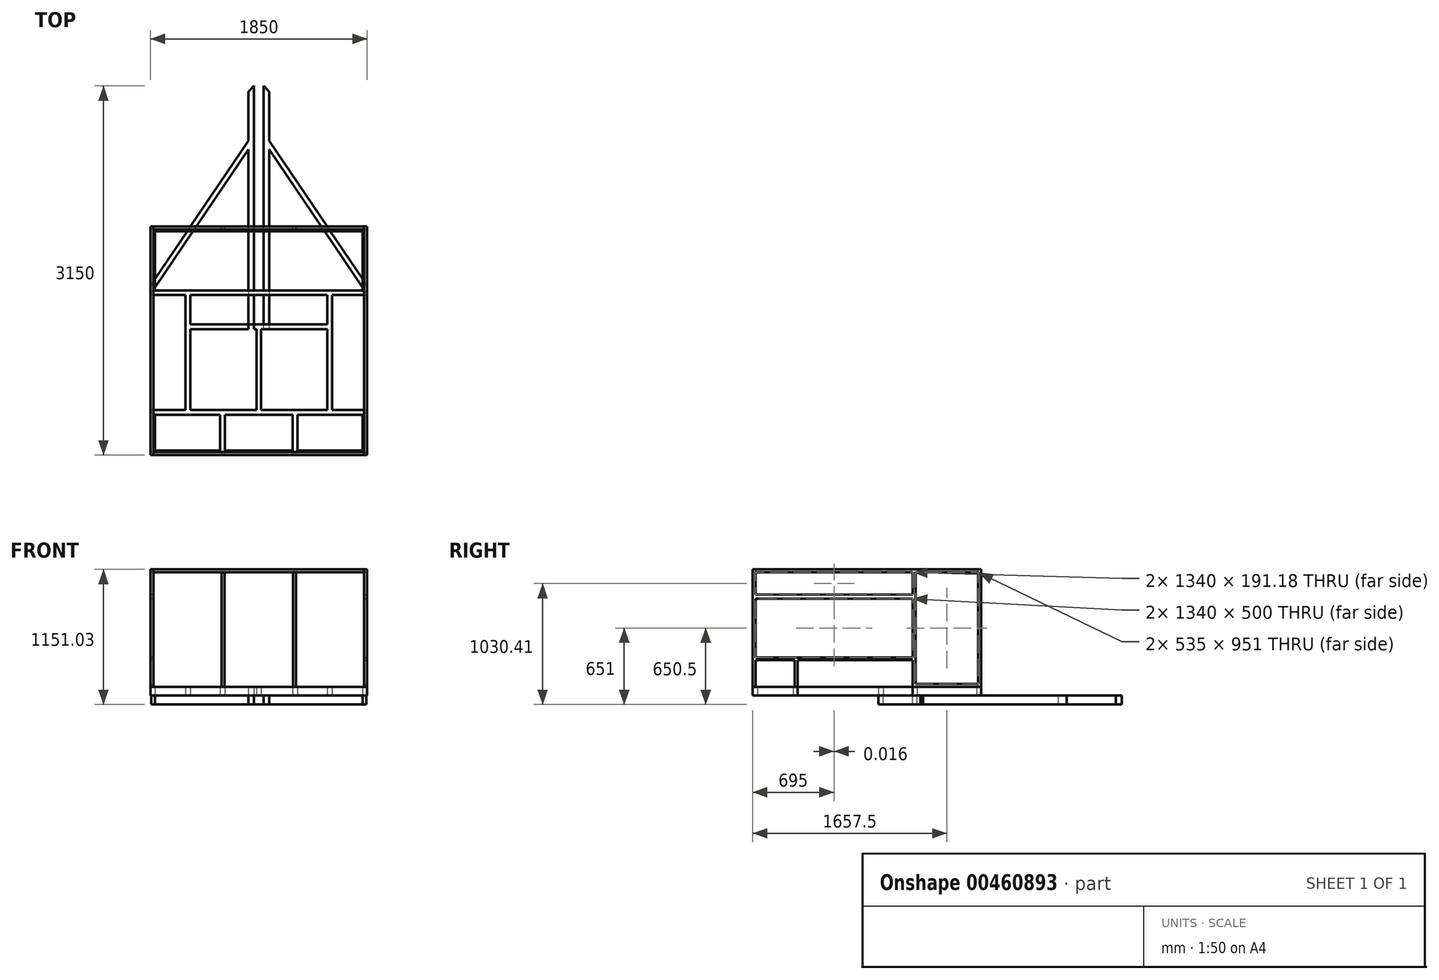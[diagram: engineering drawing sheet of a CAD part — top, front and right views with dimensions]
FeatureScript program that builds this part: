
annotation { "Feature Type Name" : "Feature", "Feature Type Description" : "" }
export const myFeature = defineFeature(function(context is Context, id is Id, definition is map)
    precondition{}
    {
        {
            var Q0;
            Q0=qCreatedBy(makeId("Top.planeOp"),FACE);
            var sketch = newSketch(context, id + "F0", { "sketchPlane" : qUnion([Q0])});
            skLineSegment(sketch, "E0.bottom", {"start": v(0, 0) * mm, "end": v(1850, 0) * mm});
            skLineSegment(sketch, "E0.top", {"start": v(0, -1950) * mm, "end": v(1850, -1950) * mm});
            skLineSegment(sketch, "E1", {"start": v(1850, -585) * mm, "end": v(1850, 0) * mm});
            skLineSegment(sketch, "E2", {"start": v(1850, -1565) * mm, "end": v(1850, -1950) * mm});
            skLineSegment(sketch, "E3", {"start": v(0, -585) * mm, "end": v(0, 0) * mm});
            skLineSegment(sketch, "E4", {"start": v(0, -1565) * mm, "end": v(0, -1950) * mm});
            skLineSegment(sketch, "E5", {"start": v(40, -40) * mm, "end": v(1810, -40) * mm});
            skLineSegment(sketch, "E6", {"start": v(1810, -40) * mm, "end": v(1810, -545) * mm});
            skLineSegment(sketch, "E7", {"start": v(1810, -1605) * mm, "end": v(1810, -1910) * mm});
            skLineSegment(sketch, "E8", {"start": v(1810, -1910) * mm, "end": v(40, -1910) * mm});
            skLineSegment(sketch, "E9", {"start": v(40, -1910) * mm, "end": v(40, -1605) * mm});
            skLineSegment(sketch, "E10", {"start": v(40, -40) * mm, "end": v(40, -545) * mm});
            skLineSegment(sketch, "E11", {"start": v(40, -545) * mm, "end": v(1810, -545) * mm});
            skLineSegment(sketch, "E12", {"start": v(0, -585) * mm, "end": v(1850, -585) * mm});
            skLineSegment(sketch, "E13", {"start": v(300, -1565) * mm, "end": v(300, -585) * mm});
            skLineSegment(sketch, "E14", {"start": v(1550, -1565) * mm, "end": v(1550, -585) * mm});
            skLineSegment(sketch, "E15", {"start": v(40, -1605) * mm, "end": v(1810, -1605) * mm});
            skLineSegment(sketch, "E16", {"start": v(0, -1565) * mm, "end": v(1850, -1565) * mm});
            skLineSegment(sketch, "E17", {"start": v(340, -585) * mm, "end": v(340, -1565) * mm});
            skLineSegment(sketch, "E18", {"start": v(1510, -585) * mm, "end": v(1510, -1565) * mm});
            skLineSegment(sketch, "E19", {"start": v(40, -518.74) * mm, "end": v(835, 659) * mm});
            skLineSegment(sketch, "E20", {"start": v(1810, -518.74) * mm, "end": v(1015, 659) * mm});
            skLineSegment(sketch, "E21", {"start": v(1810, -518.74) * mm, "end": v(1843.15, -496.36) * mm});
            skLineSegment(sketch, "E22", {"start": v(1843.15, -496.36) * mm, "end": v(1015, 730.5) * mm});
            skLineSegment(sketch, "E23", {"start": v(1015, 730.5) * mm, "end": v(1015, 659) * mm});
            skLineSegment(sketch, "E24", {"start": v(40, -518.74) * mm, "end": v(6.85, -496.36) * mm});
            skLineSegment(sketch, "E25", {"start": v(6.85, -496.36) * mm, "end": v(835, 730.5) * mm});
            skLineSegment(sketch, "E26", {"start": v(835, 730.5) * mm, "end": v(835, 659) * mm});
            skLineSegment(sketch, "E27", {"start": v(340, -835.42) * mm, "end": v(1510, -835.42) * mm});
            skLineSegment(sketch, "E28", {"start": v(340, -875.42) * mm, "end": v(1510, -875.42) * mm});
            skLineSegment(sketch, "E29", {"start": v(905, -875.42) * mm, "end": v(905, -1565) * mm});
            skLineSegment(sketch, "E30", {"start": v(945, -875.42) * mm, "end": v(945, -1565) * mm});
            skLineSegment(sketch, "E31", {"start": v(595, -1605) * mm, "end": v(595, -1910) * mm});
            skLineSegment(sketch, "E32", {"start": v(635, -1605) * mm, "end": v(635, -1910) * mm});
            skLineSegment(sketch, "E33", {"start": v(1215, -1605) * mm, "end": v(1215, -1910) * mm});
            skLineSegment(sketch, "E34", {"start": v(1255, -1605) * mm, "end": v(1255, -1910) * mm});
            skLineSegment(sketch, "E35", {"start": v(835, -875.42) * mm, "end": v(885, -875.42) * mm});
            skLineSegment(sketch, "E36", {"start": v(885, -875.42) * mm, "end": v(885, 1200) * mm});
            skLineSegment(sketch, "E37", {"start": v(965, -875.42) * mm, "end": v(965, 1200) * mm});
            skLineSegment(sketch, "E38", {"start": v(885, 1200) * mm, "end": v(835, 1150) * mm});
            skLineSegment(sketch, "E39", {"start": v(965, 1200) * mm, "end": v(1015, 1150) * mm});
            skLineSegment(sketch, "E40", {"start": v(835, 1150) * mm, "end": v(835, -875.42) * mm});
            skLineSegment(sketch, "E41", {"start": v(1015, 1150) * mm, "end": v(1015, -875.42) * mm});
            skSolve(sketch);
        }
        {
            var Q0;
            {var subQ0=sQuery(id+"F0.wireOp",EDGE,"E19");var subQ1=sQuery(id+"F0.wireOp",EDGE,"E0.bottom");var subQ2=makeQuery(id+"F0.imprint","INTERSECT",VERTEX,{"derivedFrom":[subQ1,subQ0]});Q0=makeQuery(id+"F0.imprint","IMPRINT",FACE,{"disambiguationData":[TD([[makeQuery(id+"F0.imprint","IMPRINT",EDGE,{"disambiguationData":[TD([[subQ2,-1.0]])],"derivedFrom":subQ1}),-1.0]])]});}
            var Q1;
            {var subQ0=sQuery(id+"F0.wireOp",EDGE,"E36");var subQ1=sQuery(id+"F0.wireOp",EDGE,"E0.bottom");var subQ2=makeQuery(id+"F0.imprint","INTERSECT",VERTEX,{"derivedFrom":[subQ1,subQ0]});Q1=makeQuery(id+"F0.imprint","IMPRINT",FACE,{"disambiguationData":[TD([[makeQuery(id+"F0.imprint","IMPRINT",EDGE,{"disambiguationData":[TD([[subQ2,1.0]])],"derivedFrom":subQ1}),-1.0]])]});}
            var Q2;
            {var subQ0=sQuery(id+"F0.wireOp",EDGE,"E36");var subQ1=sQuery(id+"F0.wireOp",EDGE,"E0.bottom");var subQ2=makeQuery(id+"F0.imprint","INTERSECT",VERTEX,{"derivedFrom":[subQ1,subQ0]});Q2=makeQuery(id+"F0.imprint","IMPRINT",FACE,{"disambiguationData":[TD([[makeQuery(id+"F0.imprint","IMPRINT",EDGE,{"disambiguationData":[TD([[subQ2,-1.0]])],"derivedFrom":subQ1}),-1.0]])]});}
            var Q3;
            {var subQ0=sQuery(id+"F0.wireOp",EDGE,"E37");var subQ1=sQuery(id+"F0.wireOp",EDGE,"E0.bottom");var subQ2=makeQuery(id+"F0.imprint","INTERSECT",VERTEX,{"derivedFrom":[subQ1,subQ0]});Q3=makeQuery(id+"F0.imprint","IMPRINT",FACE,{"disambiguationData":[TD([[makeQuery(id+"F0.imprint","IMPRINT",EDGE,{"disambiguationData":[TD([[subQ2,-1.0]])],"derivedFrom":subQ1}),-1.0]])]});}
            var Q4;
            {var subQ0=sQuery(id+"F0.wireOp",EDGE,"09ETFbxQ-A6C1-cuEm-suVw-SmpEZGGyVelw");var subQ1=sQuery(id+"F0.wireOp",EDGE,"E0.bottom");var subQ2=makeQuery(id+"F0.imprint","INTERSECT",VERTEX,{"derivedFrom":[subQ1,subQ0]});Q4=makeQuery(id+"F0.imprint","IMPRINT",FACE,{"disambiguationData":[TD([[makeQuery(id+"F0.imprint","IMPRINT",EDGE,{"disambiguationData":[TD([[subQ2,-1.0]])],"derivedFrom":subQ1}),-1.0]])]});}
            var Q5;
            {var subQ0=sQuery(id+"F0.wireOp",EDGE,"E25");var subQ1=sQuery(id+"F0.wireOp",EDGE,"E0.bottom");var subQ2=makeQuery(id+"F0.imprint","INTERSECT",VERTEX,{"derivedFrom":[subQ1,subQ0]});Q5=makeQuery(id+"F0.imprint","IMPRINT",FACE,{"disambiguationData":[TD([[makeQuery(id+"F0.imprint","IMPRINT",EDGE,{"disambiguationData":[TD([[subQ2,-1.0]])],"derivedFrom":subQ1}),-1.0]])]});}
            var Q6;
            {var subQ4=sQuery(id+"F0.wireOp",EDGE,"E3");Q6=makeQuery(id+"F0.imprint","IMPRINT",FACE,{"disambiguationData":[TD([[makeQuery(id+"F0.imprint","IMPRINT",EDGE,{"derivedFrom":subQ4}),-1.0]])]});}
            var Q7;
            {var subQ0=sQuery(id+"F0.wireOp",EDGE,"E22");var subQ1=sQuery(id+"F0.wireOp",EDGE,"E0.bottom");var subQ2=makeQuery(id+"F0.imprint","INTERSECT",VERTEX,{"derivedFrom":[subQ1,subQ0]});Q7=makeQuery(id+"F0.imprint","IMPRINT",FACE,{"disambiguationData":[TD([[makeQuery(id+"F0.imprint","IMPRINT",EDGE,{"disambiguationData":[TD([[subQ2,1.0]])],"derivedFrom":subQ1}),-1.0]])]});}
            var Q8;
            {var subQ1=sQuery(id+"F0.wireOp",EDGE,"E1");Q8=makeQuery(id+"F0.imprint","IMPRINT",FACE,{"disambiguationData":[TD([[makeQuery(id+"F0.imprint","IMPRINT",EDGE,{"derivedFrom":subQ1}),1.0]])]});}
            var Q9;
            {var subQ0=sQuery(id+"F0.wireOp",EDGE,"E37");var subQ1=sQuery(id+"F0.wireOp",EDGE,"E11");var subQ2=makeQuery(id+"F0.imprint","INTERSECT",VERTEX,{"derivedFrom":[subQ1,subQ0]});Q9=makeQuery(id+"F0.imprint","IMPRINT",FACE,{"disambiguationData":[TD([[makeQuery(id+"F0.imprint","IMPRINT",EDGE,{"disambiguationData":[TD([[subQ2,-1.0]])],"derivedFrom":subQ1}),-1.0]])]});}
            var Q10;
            {var subQ0=sQuery(id+"F0.wireOp",EDGE,"E36");var subQ1=sQuery(id+"F0.wireOp",EDGE,"E11");var subQ2=makeQuery(id+"F0.imprint","INTERSECT",VERTEX,{"derivedFrom":[subQ1,subQ0]});Q10=makeQuery(id+"F0.imprint","IMPRINT",FACE,{"disambiguationData":[TD([[makeQuery(id+"F0.imprint","IMPRINT",EDGE,{"disambiguationData":[TD([[subQ2,-1.0]])],"derivedFrom":subQ1}),-1.0]])]});}
            var Q11;
            {var subQ0=sQuery(id+"F0.wireOp",EDGE,"pQNNPpNY-eGQG-TIMN-oy4P-XU9trb4b4uZt");var subQ1=sQuery(id+"F0.wireOp",EDGE,"E11");var subQ2=makeQuery(id+"F0.imprint","INTERSECT",VERTEX,{"derivedFrom":[subQ1,subQ0]});Q11=makeQuery(id+"F0.imprint","IMPRINT",FACE,{"disambiguationData":[TD([[makeQuery(id+"F0.imprint","IMPRINT",EDGE,{"disambiguationData":[TD([[subQ2,-1.0]])],"derivedFrom":subQ1}),-1.0]])]});}
            var Q12;
            {var subQ0=sQuery(id+"F0.wireOp",EDGE,"E27");var subQ1=sQuery(id+"F0.wireOp",EDGE,"E17");var subQ2=makeQuery(id+"F0.imprint","INTERSECT",VERTEX,{"derivedFrom":[subQ1,subQ0]});Q12=makeQuery(id+"F0.imprint","IMPRINT",FACE,{"disambiguationData":[TD([[makeQuery(id+"F0.imprint","IMPRINT",EDGE,{"disambiguationData":[TD([[subQ2,-1.0]])],"derivedFrom":subQ1}),1.0]])]});}
            var Q13;
            {var subQ5=sQuery(id+"F0.wireOp",EDGE,"E35");Q13=makeQuery(id+"F0.imprint","IMPRINT",FACE,{"disambiguationData":[TD([[makeQuery(id+"F0.imprint","IMPRINT",EDGE,{"derivedFrom":subQ5}),1.0]])]});}
            var Q14;
            {var subQ5=sQuery(id+"F0.wireOp",EDGE,"E36");var subQ7=sQuery(id+"F0.wireOp",EDGE,"E27");var subQ8=makeQuery(id+"F0.imprint","INTERSECT",VERTEX,{"derivedFrom":[subQ7,subQ5]});Q14=makeQuery(id+"F0.imprint","IMPRINT",FACE,{"disambiguationData":[TD([[makeQuery(id+"F0.imprint","IMPRINT",EDGE,{"disambiguationData":[TD([[subQ8,-1.0]])],"derivedFrom":subQ7}),-1.0]])]});}
            var Q15;
            {var subQ0=sQuery(id+"F0.wireOp",EDGE,"E37");var subQ1=sQuery(id+"F0.wireOp",EDGE,"E27");var subQ2=makeQuery(id+"F0.imprint","INTERSECT",VERTEX,{"derivedFrom":[subQ1,subQ0]});Q15=makeQuery(id+"F0.imprint","IMPRINT",FACE,{"disambiguationData":[TD([[makeQuery(id+"F0.imprint","IMPRINT",EDGE,{"disambiguationData":[TD([[subQ2,-1.0]])],"derivedFrom":subQ1}),-1.0]])]});}
            var Q16;
            {var subQ0=sQuery(id+"F0.wireOp",EDGE,"E27");var subQ1=sQuery(id+"F0.wireOp",EDGE,"E18");var subQ2=makeQuery(id+"F0.imprint","INTERSECT",VERTEX,{"derivedFrom":[subQ1,subQ0]});Q16=makeQuery(id+"F0.imprint","IMPRINT",FACE,{"disambiguationData":[TD([[makeQuery(id+"F0.imprint","IMPRINT",EDGE,{"disambiguationData":[TD([[subQ2,-1.0]])],"derivedFrom":subQ1}),-1.0]])]});}
            var Q17;
            {var subQ5=sQuery(id+"F0.wireOp",EDGE,"E14");Q17=makeQuery(id+"F0.imprint","IMPRINT",FACE,{"disambiguationData":[TD([[makeQuery(id+"F0.imprint","IMPRINT",EDGE,{"derivedFrom":subQ5}),1.0]])]});}
            var Q18;
            {var subQ4=sQuery(id+"F0.wireOp",EDGE,"E13");Q18=makeQuery(id+"F0.imprint","IMPRINT",FACE,{"disambiguationData":[TD([[makeQuery(id+"F0.imprint","IMPRINT",EDGE,{"derivedFrom":subQ4}),-1.0]])]});}
            var Q19;
            {var subQ0=sQuery(id+"F0.wireOp",EDGE,"E29");Q19=makeQuery(id+"F0.imprint","IMPRINT",FACE,{"disambiguationData":[TD([[makeQuery(id+"F0.imprint","IMPRINT",EDGE,{"derivedFrom":subQ0}),1.0]])]});}
            var Q20;
            Q20=makeQuery(id+"F0.imprint","IMPRINT",FACE,{"disambiguationData":[TD([[makeQuery(id+"F0.imprint","IMPRINT",EDGE,{"derivedFrom":sQuery(id+"F0.wireOp",EDGE,"E0.top")}),1.0]])]});
            var Q21;
            {var subQ0=sQuery(id+"F0.wireOp",EDGE,"E31");Q21=makeQuery(id+"F0.imprint","IMPRINT",FACE,{"disambiguationData":[TD([[makeQuery(id+"F0.imprint","IMPRINT",EDGE,{"derivedFrom":subQ0}),1.0]])]});}
            var Q22;
            {var subQ0=sQuery(id+"F0.wireOp",EDGE,"E33");Q22=makeQuery(id+"F0.imprint","IMPRINT",FACE,{"disambiguationData":[TD([[makeQuery(id+"F0.imprint","IMPRINT",EDGE,{"derivedFrom":subQ0}),1.0]])]});}
            var Q23;
            {var subQ0=sQuery(id+"F0.wireOp",EDGE,"E21");Q23=makeQuery(id+"F0.imprint","IMPRINT",FACE,{"disambiguationData":[TD([[makeQuery(id+"F0.imprint","IMPRINT",EDGE,{"derivedFrom":subQ0}),1.0]])]});}
            var Q24;
            {var subQ0=sQuery(id+"F0.wireOp",EDGE,"E24");Q24=makeQuery(id+"F0.imprint","IMPRINT",FACE,{"disambiguationData":[TD([[makeQuery(id+"F0.imprint","IMPRINT",EDGE,{"derivedFrom":subQ0}),-1.0]])]});}
            extrude(context, id + "F1", {"entities" : qUnion([Q0, Q1, Q2, Q3, Q4, Q5, Q6, Q7, Q8, Q9, Q10, Q11, Q12, Q13, Q14, Q15, Q16, Q17, Q18, Q19, Q20, Q21, Q22, Q23, Q24]), "depth" : 75 * mm});
        }
        {
            var Q0;
            {var subQ0=sQuery(id+"F0.wireOp",EDGE,"E37");var subQ1=sQuery(id+"F0.wireOp",EDGE,"E12");var subQ2=makeQuery(id+"F0.imprint","INTERSECT",VERTEX,{"derivedFrom":[subQ1,subQ0]});Q0=makeQuery(id+"F0.imprint","IMPRINT",FACE,{"disambiguationData":[TD([[makeQuery(id+"F0.imprint","IMPRINT",EDGE,{"disambiguationData":[TD([[subQ2,-1.0]])],"derivedFrom":subQ1}),-1.0]])]});}
            var Q1;
            {var subQ0=sQuery(id+"F0.wireOp",EDGE,"E25");var subQ1=sQuery(id+"F0.wireOp",EDGE,"E0.bottom");var subQ2=makeQuery(id+"F0.imprint","INTERSECT",VERTEX,{"derivedFrom":[subQ1,subQ0]});Q1=makeQuery(id+"F0.imprint","IMPRINT",FACE,{"disambiguationData":[TD([[makeQuery(id+"F0.imprint","IMPRINT",EDGE,{"disambiguationData":[TD([[subQ2,-1.0]])],"derivedFrom":subQ1}),1.0]])]});}
            var Q2;
            {var subQ0=sQuery(id+"F0.wireOp",EDGE,"E25");var subQ1=sQuery(id+"F0.wireOp",EDGE,"E5");var subQ2=makeQuery(id+"F0.imprint","INTERSECT",VERTEX,{"derivedFrom":[subQ1,subQ0]});Q2=makeQuery(id+"F0.imprint","IMPRINT",FACE,{"disambiguationData":[TD([[makeQuery(id+"F0.imprint","IMPRINT",EDGE,{"disambiguationData":[TD([[subQ2,-1.0]])],"derivedFrom":subQ1}),-1.0]])]});}
            var Q3;
            {var subQ0=sQuery(id+"F0.wireOp",EDGE,"E25");var subQ1=sQuery(id+"F0.wireOp",EDGE,"E0.bottom");var subQ2=makeQuery(id+"F0.imprint","INTERSECT",VERTEX,{"derivedFrom":[subQ1,subQ0]});Q3=makeQuery(id+"F0.imprint","IMPRINT",FACE,{"disambiguationData":[TD([[makeQuery(id+"F0.imprint","IMPRINT",EDGE,{"disambiguationData":[TD([[subQ2,-1.0]])],"derivedFrom":subQ1}),-1.0]])]});}
            var Q4;
            {var subQ0=sQuery(id+"F0.wireOp",EDGE,"E37");var subQ1=sQuery(id+"F0.wireOp",EDGE,"E5");var subQ2=makeQuery(id+"F0.imprint","INTERSECT",VERTEX,{"derivedFrom":[subQ1,subQ0]});Q4=makeQuery(id+"F0.imprint","IMPRINT",FACE,{"disambiguationData":[TD([[makeQuery(id+"F0.imprint","IMPRINT",EDGE,{"disambiguationData":[TD([[subQ2,-1.0]])],"derivedFrom":subQ1}),-1.0]])]});}
            var Q5;
            {var subQ0=sQuery(id+"F0.wireOp",EDGE,"E20");var subQ1=sQuery(id+"F0.wireOp",EDGE,"E5");var subQ2=makeQuery(id+"F0.imprint","INTERSECT",VERTEX,{"derivedFrom":[subQ1,subQ0]});Q5=makeQuery(id+"F0.imprint","IMPRINT",FACE,{"disambiguationData":[TD([[makeQuery(id+"F0.imprint","IMPRINT",EDGE,{"disambiguationData":[TD([[subQ2,-1.0]])],"derivedFrom":subQ1}),-1.0]])]});}
            var Q6;
            {var subQ0=sQuery(id+"F0.wireOp",EDGE,"E22");var subQ1=sQuery(id+"F0.wireOp",EDGE,"E0.bottom");var subQ2=makeQuery(id+"F0.imprint","INTERSECT",VERTEX,{"derivedFrom":[subQ1,subQ0]});Q6=makeQuery(id+"F0.imprint","IMPRINT",FACE,{"disambiguationData":[TD([[makeQuery(id+"F0.imprint","IMPRINT",EDGE,{"disambiguationData":[TD([[subQ2,1.0]])],"derivedFrom":subQ1}),1.0]])]});}
            var Q7;
            {var subQ0=sQuery(id+"F0.wireOp",EDGE,"E22");var subQ1=sQuery(id+"F0.wireOp",EDGE,"E0.bottom");var subQ2=makeQuery(id+"F0.imprint","INTERSECT",VERTEX,{"derivedFrom":[subQ1,subQ0]});Q7=makeQuery(id+"F0.imprint","IMPRINT",FACE,{"disambiguationData":[TD([[makeQuery(id+"F0.imprint","IMPRINT",EDGE,{"disambiguationData":[TD([[subQ2,1.0]])],"derivedFrom":subQ1}),-1.0]])]});}
            var Q8;
            {var subQ0=sQuery(id+"F0.wireOp",EDGE,"E37");var subQ1=sQuery(id+"F0.wireOp",EDGE,"E0.bottom");var subQ2=makeQuery(id+"F0.imprint","INTERSECT",VERTEX,{"derivedFrom":[subQ1,subQ0]});Q8=makeQuery(id+"F0.imprint","IMPRINT",FACE,{"disambiguationData":[TD([[makeQuery(id+"F0.imprint","IMPRINT",EDGE,{"disambiguationData":[TD([[subQ2,-1.0]])],"derivedFrom":subQ1}),-1.0]])]});}
            var Q9;
            {var subQ0=sQuery(id+"F0.wireOp",EDGE,"E36");var subQ1=sQuery(id+"F0.wireOp",EDGE,"E0.bottom");var subQ2=makeQuery(id+"F0.imprint","INTERSECT",VERTEX,{"derivedFrom":[subQ1,subQ0]});Q9=makeQuery(id+"F0.imprint","IMPRINT",FACE,{"disambiguationData":[TD([[makeQuery(id+"F0.imprint","IMPRINT",EDGE,{"disambiguationData":[TD([[subQ2,1.0]])],"derivedFrom":subQ1}),-1.0]])]});}
            var Q10;
            {var subQ0=sQuery(id+"F0.wireOp",EDGE,"E40");var subQ1=sQuery(id+"F0.wireOp",EDGE,"E11");var subQ2=makeQuery(id+"F0.imprint","INTERSECT",VERTEX,{"derivedFrom":[subQ1,subQ0]});Q10=makeQuery(id+"F0.imprint","IMPRINT",FACE,{"disambiguationData":[TD([[makeQuery(id+"F0.imprint","IMPRINT",EDGE,{"disambiguationData":[TD([[subQ2,-1.0]])],"derivedFrom":subQ1}),-1.0]])]});}
            var Q11;
            {var subQ0=sQuery(id+"F0.wireOp",EDGE,"E36");var subQ1=sQuery(id+"F0.wireOp",EDGE,"E11");var subQ2=makeQuery(id+"F0.imprint","INTERSECT",VERTEX,{"derivedFrom":[subQ1,subQ0]});Q11=makeQuery(id+"F0.imprint","IMPRINT",FACE,{"disambiguationData":[TD([[makeQuery(id+"F0.imprint","IMPRINT",EDGE,{"disambiguationData":[TD([[subQ2,-1.0]])],"derivedFrom":subQ1}),-1.0]])]});}
            var Q12;
            {var subQ0=sQuery(id+"F0.wireOp",EDGE,"E37");var subQ1=sQuery(id+"F0.wireOp",EDGE,"E11");var subQ2=makeQuery(id+"F0.imprint","INTERSECT",VERTEX,{"derivedFrom":[subQ1,subQ0]});Q12=makeQuery(id+"F0.imprint","IMPRINT",FACE,{"disambiguationData":[TD([[makeQuery(id+"F0.imprint","IMPRINT",EDGE,{"disambiguationData":[TD([[subQ2,-1.0]])],"derivedFrom":subQ1}),-1.0]])]});}
            var Q13;
            {var subQ0=sQuery(id+"F0.wireOp",EDGE,"E37");var subQ1=sQuery(id+"F0.wireOp",EDGE,"E12");var subQ2=makeQuery(id+"F0.imprint","INTERSECT",VERTEX,{"derivedFrom":[subQ1,subQ0]});Q13=makeQuery(id+"F0.imprint","IMPRINT",FACE,{"disambiguationData":[TD([[makeQuery(id+"F0.imprint","IMPRINT",EDGE,{"disambiguationData":[TD([[subQ2,-1.0]])],"derivedFrom":subQ1}),-1.0]])]});}
            var Q14;
            {var subQ5=sQuery(id+"F0.wireOp",EDGE,"E35");Q14=makeQuery(id+"F0.imprint","IMPRINT",FACE,{"disambiguationData":[TD([[makeQuery(id+"F0.imprint","IMPRINT",EDGE,{"derivedFrom":subQ5}),1.0]])]});}
            var Q15;
            {var subQ0=sQuery(id+"F0.wireOp",EDGE,"E37");var subQ1=sQuery(id+"F0.wireOp",EDGE,"E27");var subQ2=makeQuery(id+"F0.imprint","INTERSECT",VERTEX,{"derivedFrom":[subQ1,subQ0]});Q15=makeQuery(id+"F0.imprint","IMPRINT",FACE,{"disambiguationData":[TD([[makeQuery(id+"F0.imprint","IMPRINT",EDGE,{"disambiguationData":[TD([[subQ2,-1.0]])],"derivedFrom":subQ1}),-1.0]])]});}
            var Q16;
            {var subQ0=sQuery(id+"F0.wireOp",EDGE,"E24");Q16=makeQuery(id+"F0.imprint","IMPRINT",FACE,{"disambiguationData":[TD([[makeQuery(id+"F0.imprint","IMPRINT",EDGE,{"derivedFrom":subQ0}),-1.0]])]});}
            var Q17;
            {var subQ0=sQuery(id+"F0.wireOp",EDGE,"E37");var subQ1=sQuery(id+"F0.wireOp",EDGE,"E11");var subQ2=makeQuery(id+"F0.imprint","INTERSECT",VERTEX,{"derivedFrom":[subQ1,subQ0]});Q17=makeQuery(id+"F0.imprint","IMPRINT",FACE,{"disambiguationData":[TD([[makeQuery(id+"F0.imprint","IMPRINT",EDGE,{"disambiguationData":[TD([[subQ2,-1.0]])],"derivedFrom":subQ1}),-1.0]])]});}
            var Q18;
            {var subQ0=sQuery(id+"F0.wireOp",EDGE,"E21");Q18=makeQuery(id+"F0.imprint","IMPRINT",FACE,{"disambiguationData":[TD([[makeQuery(id+"F0.imprint","IMPRINT",EDGE,{"derivedFrom":subQ0}),1.0]])]});}
            var Q19;
            {var subQ0=sQuery(id+"F0.wireOp",EDGE,"E40");var subQ1=sQuery(id+"F0.wireOp",EDGE,"E5");var subQ2=makeQuery(id+"F0.imprint","INTERSECT",VERTEX,{"derivedFrom":[subQ1,subQ0]});Q19=makeQuery(id+"F0.imprint","IMPRINT",FACE,{"disambiguationData":[TD([[makeQuery(id+"F0.imprint","IMPRINT",EDGE,{"disambiguationData":[TD([[subQ2,-1.0]])],"derivedFrom":subQ1}),-1.0]])]});}
            var Q20;
            {var subQ0=sQuery(id+"F0.wireOp",EDGE,"E40");var subQ1=sQuery(id+"F0.wireOp",EDGE,"E12");var subQ2=makeQuery(id+"F0.imprint","INTERSECT",VERTEX,{"derivedFrom":[subQ1,subQ0]});Q20=makeQuery(id+"F0.imprint","IMPRINT",FACE,{"disambiguationData":[TD([[makeQuery(id+"F0.imprint","IMPRINT",EDGE,{"disambiguationData":[TD([[subQ2,-1.0]])],"derivedFrom":subQ1}),-1.0]])]});}
            var Q21;
            {var subQ0=sQuery(id+"F0.wireOp",EDGE,"E38");Q21=makeQuery(id+"F0.imprint","IMPRINT",FACE,{"disambiguationData":[TD([[makeQuery(id+"F0.imprint","IMPRINT",EDGE,{"derivedFrom":subQ0}),1.0]])]});}
            var Q22;
            {var subQ2=sQuery(id+"F0.wireOp",EDGE,"E39");Q22=makeQuery(id+"F0.imprint","IMPRINT",FACE,{"disambiguationData":[TD([[makeQuery(id+"F0.imprint","IMPRINT",EDGE,{"derivedFrom":subQ2}),-1.0]])]});}
            extrude(context, id + "F2", {"entities" : qUnion([Q0, Q1, Q2, Q3, Q4, Q5, Q6, Q7, Q8, Q9, Q10, Q11, Q12, Q13, Q14, Q15, Q16, Q17, Q18, Q19, Q20, Q21, Q22]), "oppositeDirection" : true, "depth" : 75 * mm});
        }
        {
            var Q0;
            Q0=qCreatedBy(makeId("Right.planeOp"),FACE);
            var sketch = newSketch(context, id + "F3", { "sketchPlane" : qUnion([Q0])});
            skLineSegment(sketch, "E42.top", {"start": v(0, 1076) * mm, "end": v(-1950, 1076) * mm});
            skLineSegment(sketch, "E42.left", {"start": v(0, 75) * mm, "end": v(0, 1076) * mm});
            skLineSegment(sketch, "E42.right", {"start": v(-1950, 76) * mm, "end": v(-1950, 1076) * mm});
            skLineSegment(sketch, "E43.bottom", {"start": v(-25, 1051) * mm, "end": v(-1925, 1051) * mm});
            skLineSegment(sketch, "E43.left", {"start": v(-25, 1051) * mm, "end": v(-25, 100) * mm});
            skLineSegment(sketch, "E43.right", {"start": v(-1925, 1051) * mm, "end": v(-1925, 76) * mm});
            skLineSegment(sketch, "E44", {"start": v(-585, 75) * mm, "end": v(-585, 1051) * mm});
            skLineSegment(sketch, "E45", {"start": v(-25, 100) * mm, "end": v(-560, 100) * mm});
            skLineSegment(sketch, "E46", {"start": v(-560, 100) * mm, "end": v(-560, 1051) * mm});
            skLineSegment(sketch, "E47", {"start": v(-585, 326) * mm, "end": v(-1925, 326) * mm});
            skLineSegment(sketch, "E48", {"start": v(-585, 301) * mm, "end": v(-1925, 301) * mm});
            skLineSegment(sketch, "E49", {"start": v(-585, 75) * mm, "end": v(0, 75) * mm});
            skLineSegment(sketch, "E50", {"start": v(-1925, 76) * mm, "end": v(-1950, 76) * mm});
            skLineSegment(sketch, "E51", {"start": v(-1565, 75.02) * mm, "end": v(-1565, 301) * mm});
            skLineSegment(sketch, "E52", {"start": v(-1565, 301) * mm, "end": v(-1590, 301) * mm});
            skLineSegment(sketch, "E53", {"start": v(-1590, 301) * mm, "end": v(-1590, 75.02) * mm});
            skLineSegment(sketch, "E54", {"start": v(-1590, 75.02) * mm, "end": v(-1565, 75.02) * mm});
            skLineSegment(sketch, "E55", {"start": v(-585, 826) * mm, "end": v(-1925, 826) * mm});
            skLineSegment(sketch, "E56", {"start": v(-585, 826) * mm, "end": v(-585, 859.82) * mm});
            skLineSegment(sketch, "E57", {"start": v(-585, 859.82) * mm, "end": v(-1925, 859.82) * mm});
            skLineSegment(sketch, "E58", {"start": v(-1925, 859.82) * mm, "end": v(-1925, 826) * mm});
            skSolve(sketch);
        }
        {
            var Q0;
            Q0=makeQuery(id+"F3.imprint","IMPRINT",FACE,{"disambiguationData":[TD([[makeQuery(id+"F3.imprint","IMPRINT",EDGE,{"derivedFrom":sQuery(id+"F3.wireOp",EDGE,"E42.top")}),1.0]])]});
            var Q1;
            {var subQ0=sQuery(id+"F3.wireOp",EDGE,"E47");Q1=makeQuery(id+"F3.imprint","IMPRINT",FACE,{"disambiguationData":[TD([[makeQuery(id+"F3.imprint","IMPRINT",EDGE,{"derivedFrom":subQ0}),1.0]])]});}
            var Q2;
            Q2=makeQuery(id+"F3.imprint","IMPRINT",FACE,{"disambiguationData":[TD([[makeQuery(id+"F3.imprint","IMPRINT",EDGE,{"derivedFrom":sQuery(id+"F3.wireOp",EDGE,"E51")}),1.0]])]});
            var Q3;
            Q3=makeQuery(id+"F3.imprint","IMPRINT",FACE,{"disambiguationData":[TD([[makeQuery(id+"F3.imprint","IMPRINT",EDGE,{"derivedFrom":sQuery(id+"F3.wireOp",EDGE,"E55")}),-1.0]])]});
            extrude(context, id + "F4", {"entities" : qUnion([Q0, Q1, Q2, Q3]), "depth" : 25 * mm});
        }
        {
            var Q0;
            Q0=qCreatedBy(makeId("Right.planeOp"),FACE);
            cPlane(context, id + "F5", {"entities" : qUnion([Q0]), "cplaneType" : CPlaneType.OFFSET, "offset" : 1850 * mm, "width" : 150 * mm, "height" : 150 * mm});
        }
        {
            var Q0;
            Q0=qCreatedBy(makeId("Front.planeOp"),FACE);
            cPlane(context, id + "F6", {"entities" : qUnion([Q0]), "cplaneType" : CPlaneType.OFFSET, "offset" : 1950 * mm, "width" : 150 * mm, "height" : 150 * mm});
        }
        {
            var Q0;
            Q0=qCreatedBy(id+"F5.planeOp",FACE);
            var sketch = newSketch(context, id + "F7", { "sketchPlane" : qUnion([Q0])});
            skLineSegment(sketch, "E59.top", {"start": v(0.02, 1076.03) * mm, "end": v(-1949.98, 1076.03) * mm});
            skLineSegment(sketch, "E59.left", {"start": v(0.02, 75.04) * mm, "end": v(0.02, 1076.03) * mm});
            skLineSegment(sketch, "E59.right", {"start": v(-1949.98, 76.03) * mm, "end": v(-1949.98, 1076.03) * mm});
            skLineSegment(sketch, "E60.bottom", {"start": v(-24.98, 1051.03) * mm, "end": v(-1924.98, 1051.03) * mm});
            skLineSegment(sketch, "E60.left", {"start": v(-24.98, 1051.03) * mm, "end": v(-24.98, 100.03) * mm});
            skLineSegment(sketch, "E60.right", {"start": v(-1924.98, 1051.03) * mm, "end": v(-1924.98, 76.03) * mm});
            skLineSegment(sketch, "E61", {"start": v(-584.98, 75.04) * mm, "end": v(-584.98, 1051.03) * mm});
            skLineSegment(sketch, "E62", {"start": v(-24.98, 100.03) * mm, "end": v(-559.98, 100.03) * mm});
            skLineSegment(sketch, "E63", {"start": v(-559.98, 100.03) * mm, "end": v(-559.98, 1051.03) * mm});
            skLineSegment(sketch, "E64", {"start": v(-584.98, 326.03) * mm, "end": v(-1924.98, 326.03) * mm});
            skLineSegment(sketch, "E65", {"start": v(-584.98, 301.03) * mm, "end": v(-1924.98, 301.03) * mm});
            skLineSegment(sketch, "E66", {"start": v(-584.98, 75.04) * mm, "end": v(0.02, 75.04) * mm});
            skLineSegment(sketch, "E67", {"start": v(-1924.98, 76.03) * mm, "end": v(-1949.98, 76.03) * mm});
            skLineSegment(sketch, "E68", {"start": v(-1564.98, 75.05) * mm, "end": v(-1564.98, 301.03) * mm});
            skLineSegment(sketch, "E69", {"start": v(-1564.98, 301.03) * mm, "end": v(-1589.98, 301.03) * mm});
            skLineSegment(sketch, "E70", {"start": v(-1589.98, 301.03) * mm, "end": v(-1589.98, 75.05) * mm});
            skLineSegment(sketch, "E71", {"start": v(-1589.98, 75.05) * mm, "end": v(-1564.98, 75.05) * mm});
            skLineSegment(sketch, "E72", {"start": v(-584.98, 826.03) * mm, "end": v(-1924.98, 826.03) * mm});
            skLineSegment(sketch, "E73", {"start": v(-584.98, 826.03) * mm, "end": v(-584.98, 859.86) * mm});
            skLineSegment(sketch, "E74", {"start": v(-584.98, 859.86) * mm, "end": v(-1924.98, 859.86) * mm});
            skLineSegment(sketch, "E75", {"start": v(-1924.98, 859.86) * mm, "end": v(-1924.98, 826.03) * mm});
            skSolve(sketch);
        }
        {
            var Q0;
            Q0=makeQuery(id+"F7.imprint","IMPRINT",FACE,{"disambiguationData":[TD([[makeQuery(id+"F7.imprint","IMPRINT",EDGE,{"derivedFrom":sQuery(id+"F7.wireOp",EDGE,"E72")}),-1.0]])]});
            var Q1;
            Q1=makeQuery(id+"F7.imprint","IMPRINT",FACE,{"disambiguationData":[TD([[makeQuery(id+"F7.imprint","IMPRINT",EDGE,{"derivedFrom":sQuery(id+"F7.wireOp",EDGE,"E59.top")}),1.0]])]});
            var Q2;
            {var subQ4=sQuery(id+"F7.wireOp",EDGE,"E64");Q2=makeQuery(id+"F7.imprint","IMPRINT",FACE,{"disambiguationData":[TD([[makeQuery(id+"F7.imprint","IMPRINT",EDGE,{"derivedFrom":subQ4}),1.0]])]});}
            var Q3;
            Q3=makeQuery(id+"F7.imprint","IMPRINT",FACE,{"disambiguationData":[TD([[makeQuery(id+"F7.imprint","IMPRINT",EDGE,{"derivedFrom":sQuery(id+"F7.wireOp",EDGE,"E68")}),1.0]])]});
            extrude(context, id + "F8", {"entities" : qUnion([Q0, Q1, Q2, Q3]), "oppositeDirection" : true, "depth" : 25 * mm});
        }
        {
            var Q0;
            Q0=qCreatedBy(makeId("Front.planeOp"),FACE);
            var sketch = newSketch(context, id + "F9", { "sketchPlane" : qUnion([Q0])});
            skLineSegment(sketch, "E76", {"start": v(608.29, 75.26) * mm, "end": v(608.29, 1050.9) * mm});
            skLineSegment(sketch, "E77", {"start": v(633.29, 1050.9) * mm, "end": v(633.29, 75.26) * mm});
            skLineSegment(sketch, "E78", {"start": v(1216.59, 1050.9) * mm, "end": v(1216.59, 75.26) * mm});
            skLineSegment(sketch, "E79", {"start": v(1241.59, 75.26) * mm, "end": v(1241.59, 1050.9) * mm});
            skLineSegment(sketch, "E80", {"start": v(25, 1050.96) * mm, "end": v(1824.98, 1050.96) * mm});
            skLineSegment(sketch, "E81", {"start": v(1824.98, 1050.96) * mm, "end": v(1824.98, 1076) * mm});
            skLineSegment(sketch, "E82", {"start": v(1824.98, 1076) * mm, "end": v(25, 1075.96) * mm});
            skLineSegment(sketch, "E83", {"start": v(25, 1075.96) * mm, "end": v(25, 1050.96) * mm});
            skLineSegment(sketch, "E84", {"start": v(608.29, 75.26) * mm, "end": v(633.29, 75.26) * mm});
            skLineSegment(sketch, "E85", {"start": v(1216.59, 75.26) * mm, "end": v(1241.59, 75.26) * mm});
            skLineSegment(sketch, "E86", {"start": v(608.29, 1050.9) * mm, "end": v(633.29, 1050.9) * mm});
            skLineSegment(sketch, "E87", {"start": v(1216.59, 1050.9) * mm, "end": v(1241.59, 1050.9) * mm});
            skSolve(sketch);
        }
        {
            var Q0;
            Q0=makeQuery(id+"F9.imprint","IMPRINT",FACE,{"disambiguationData":[TD([[makeQuery(id+"F9.imprint","IMPRINT",EDGE,{"derivedFrom":sQuery(id+"F9.wireOp",EDGE,"E78")}),1.0]])]});
            var Q1;
            Q1=makeQuery(id+"F9.imprint","IMPRINT",FACE,{"disambiguationData":[TD([[makeQuery(id+"F9.imprint","IMPRINT",EDGE,{"derivedFrom":sQuery(id+"F9.wireOp",EDGE,"E76")}),-1.0]])]});
            var Q2;
            Q2=makeQuery(id+"F9.imprint","IMPRINT",FACE,{"disambiguationData":[TD([[makeQuery(id+"F9.imprint","IMPRINT",EDGE,{"derivedFrom":sQuery(id+"F9.wireOp",EDGE,"E80")}),1.0]])]});
            extrude(context, id + "F10", {"entities" : qUnion([Q0, Q1, Q2]), "depth" : 25 * mm});
        }
        {
            var Q0;
            Q0=qCreatedBy(id+"F6.planeOp",FACE);
            var sketch = newSketch(context, id + "F11", { "sketchPlane" : qUnion([Q0])});
            skLineSegment(sketch, "E88", {"start": v(608.3, 75.28) * mm, "end": v(608.3, 1050.92) * mm});
            skLineSegment(sketch, "E89", {"start": v(633.3, 1050.92) * mm, "end": v(633.3, 75.28) * mm});
            skLineSegment(sketch, "E90", {"start": v(1216.6, 1050.92) * mm, "end": v(1216.6, 75.28) * mm});
            skLineSegment(sketch, "E91", {"start": v(1241.6, 75.28) * mm, "end": v(1241.6, 1050.92) * mm});
            skLineSegment(sketch, "E92", {"start": v(25, 1050.98) * mm, "end": v(1825, 1050.98) * mm});
            skLineSegment(sketch, "E93", {"start": v(1825, 1050.98) * mm, "end": v(1825, 1076.03) * mm});
            skLineSegment(sketch, "E94", {"start": v(1825, 1076.03) * mm, "end": v(25.02, 1075.98) * mm});
            skLineSegment(sketch, "E95", {"start": v(25.02, 1075.98) * mm, "end": v(25, 1050.98) * mm});
            skLineSegment(sketch, "E96", {"start": v(608.3, 75.28) * mm, "end": v(633.3, 75.28) * mm});
            skLineSegment(sketch, "E97", {"start": v(1216.6, 75.28) * mm, "end": v(1241.6, 75.28) * mm});
            skLineSegment(sketch, "E98", {"start": v(608.3, 1050.92) * mm, "end": v(633.3, 1050.92) * mm});
            skLineSegment(sketch, "E99", {"start": v(1216.6, 1050.92) * mm, "end": v(1241.6, 1050.92) * mm});
            skSolve(sketch);
        }
        {
            var Q0;
            Q0=makeQuery(id+"F11.imprint","IMPRINT",FACE,{"disambiguationData":[TD([[makeQuery(id+"F11.imprint","IMPRINT",EDGE,{"derivedFrom":sQuery(id+"F11.wireOp",EDGE,"E92")}),1.0]])]});
            var Q1;
            Q1=makeQuery(id+"F11.imprint","IMPRINT",FACE,{"disambiguationData":[TD([[makeQuery(id+"F11.imprint","IMPRINT",EDGE,{"derivedFrom":sQuery(id+"F11.wireOp",EDGE,"E88")}),-1.0]])]});
            var Q2;
            Q2=makeQuery(id+"F11.imprint","IMPRINT",FACE,{"disambiguationData":[TD([[makeQuery(id+"F11.imprint","IMPRINT",EDGE,{"derivedFrom":sQuery(id+"F11.wireOp",EDGE,"E90")}),1.0]])]});
            extrude(context, id + "F12", {"entities" : qUnion([Q0, Q1, Q2]), "oppositeDirection" : true, "depth" : 25 * mm});
        }
    });
